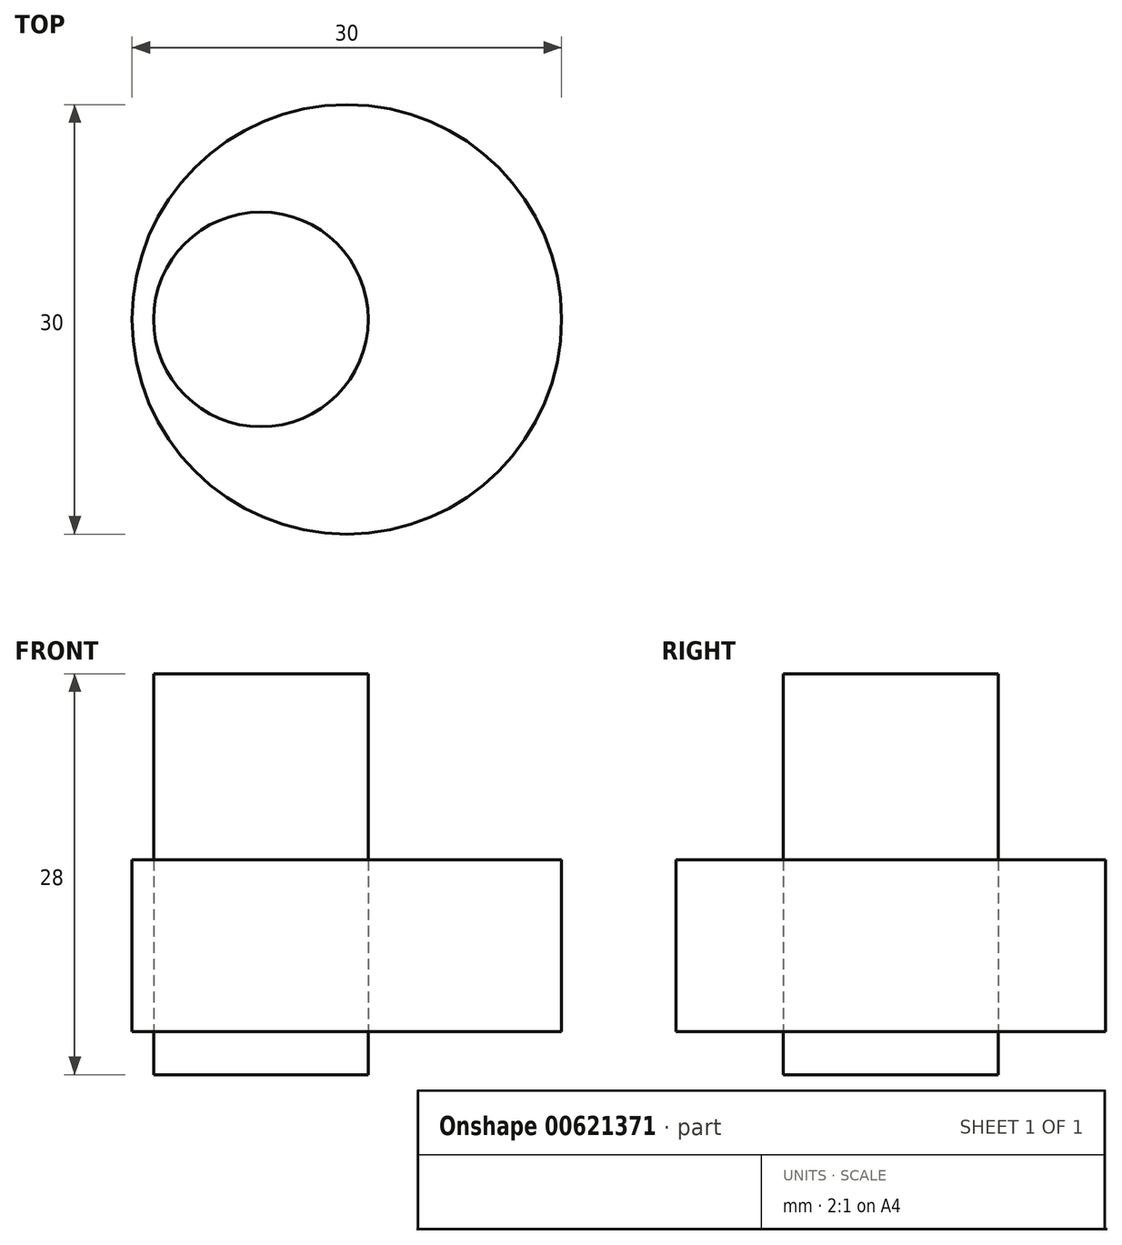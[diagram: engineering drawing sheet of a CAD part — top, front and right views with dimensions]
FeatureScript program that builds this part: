
annotation { "Feature Type Name" : "Feature", "Feature Type Description" : "" }
export const myFeature = defineFeature(function(context is Context, id is Id, definition is map)
    precondition{}
    {
        {
            var Q0;
            Q0=qCreatedBy(makeId("Top.planeOp"),FACE);
            var sketch = newSketch(context, id + "F0", { "sketchPlane" : qUnion([Q0])});
            skCircle(sketch, "E0", {"center": v(0, 0) * mm, "radius": 7.5 * mm});
            skSolve(sketch);
        }
        {
            var Q0;
            Q0 = qSketchRegion(id + "F0", true);
            extrude(context, id + "F1", {"entities" : qUnion([Q0]), "depth" : 3 * mm, "offsetDistance" : 25 * mm});
        }
        {
            var Q0;
            Q0=makeQuery(id+"F1.opExtrude","CAP_FACE",FACE,{"disambiguationData":[OSD([sQuery(id+"F0.wireOp",EDGE,"E0")])],"isStart":false});
            var sketch = newSketch(context, id + "F2", { "sketchPlane" : qUnion([Q0])});
            skCircle(sketch, "E1", {"center": v(0, 0) * mm, "radius": 7.5 * mm});
            skCircle(sketch, "E2", {"center": v(6, 0) * mm, "radius": 15 * mm});
            skSolve(sketch);
        }
        {
            var Q0;
            Q0 = qSketchRegion(id + "F2", true);
            extrude(context, id + "F3", {"entities" : qUnion([Q0]), "depth" : 12 * mm, "offsetDistance" : 25 * mm});
        }
        {
            var Q0;
            Q0=makeQuery(id+"F1.opExtrude","CAP_FACE",FACE,{"disambiguationData":[OSD([sQuery(id+"F0.wireOp",EDGE,"E0")])],"isStart":false});
            var sketch = newSketch(context, id + "F4", { "sketchPlane" : qUnion([Q0])});
            skCircle(sketch, "E3", {"center": v(0, 0) * mm, "radius": 7.5 * mm});
            skSolve(sketch);
        }
        {
            var Q0;
            Q0 = qSketchRegion(id + "F4", true);
            extrude(context, id + "F5", {"entities" : qUnion([Q0]), "depth" : 25 * mm, "offsetDistance" : 25 * mm});
        }
    });
